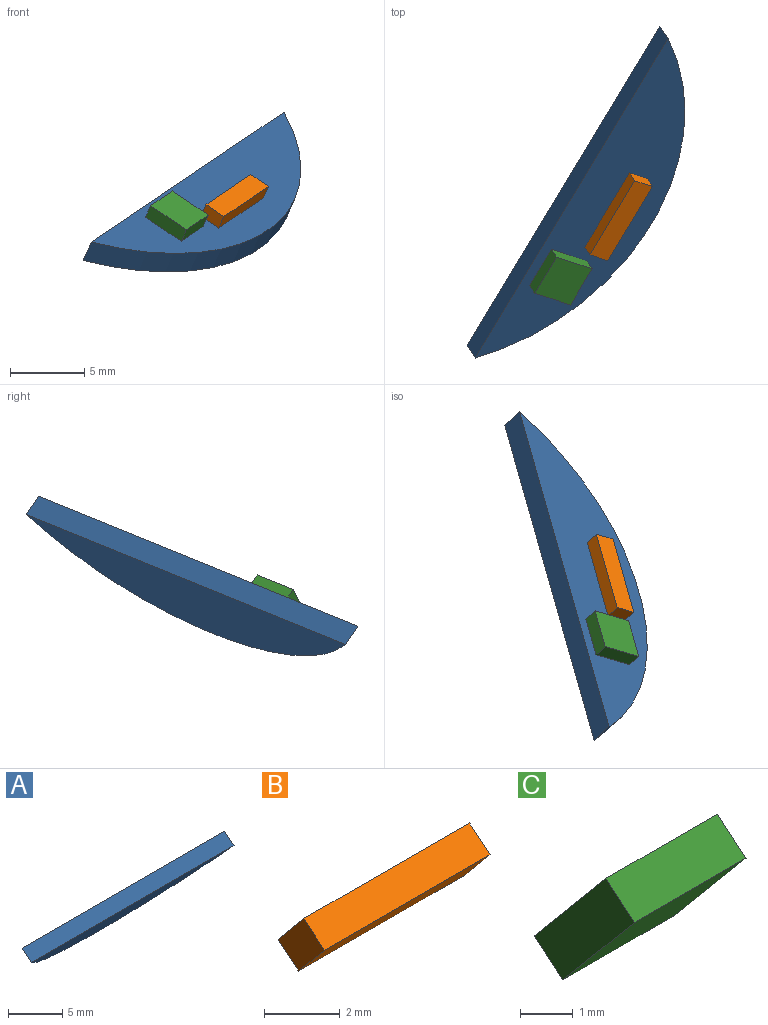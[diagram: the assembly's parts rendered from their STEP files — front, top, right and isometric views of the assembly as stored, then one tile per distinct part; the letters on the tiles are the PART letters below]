
ASSEMBLY  parts=3 mates=2
PART A: 4 faces, bbox 26.5x5.5x6.1 mm
  f0: cylinder r=16.5mm len=26.53mm, axis (0,0.77,0.64), area 49.3mm2, adj f1,f2,f3
  f1: plane 26.53x1.23mm, normal (0,-0.64,0.77), area 42.4mm2, adj f0,f2,f3
  f2: plane 26.53x5.12mm, normal (0,-0.77,-0.64), area 124mm2, adj f0,f1
  f3: plane 26.53x5.12mm, normal (0,0.77,0.64), area 124mm2, adj f0,f1
PART B: 6 faces, bbox 6.2x1.7x1.8 mm
  f0: plane 1.79x1.73mm, normal (1,0,0), area 1.5mm2, adj f1,f3,f4,f5
  f1: plane 6.16x0.77mm, normal (0,0.64,-0.77), area 6.2mm2, adj f0,f2,f4,f5
  f2: plane 1.79x1.73mm, normal (-1,0,0), area 1.5mm2, adj f1,f3,f4,f5
  f3: plane 6.16x0.77mm, normal (0,-0.64,0.77), area 6.2mm2, adj f0,f2,f4,f5
  f4: plane 6.16x1.15mm, normal (0,0.77,0.64), area 9.2mm2, adj f0,f1,f2,f3
  f5: plane 6.16x1.15mm, normal (0,-0.77,-0.64), area 9.2mm2, adj f0,f1,f2,f3
PART C: 6 faces, bbox 3x2.7x2.9 mm
  f0: plane 3x0.77mm, normal (0,0.64,-0.77), area 3mm2, adj f1,f3,f4,f5
  f1: plane 2.94x2.69mm, normal (-1,0,0), area 3mm2, adj f0,f2,f4,f5
  f2: plane 3x0.77mm, normal (0,-0.64,0.77), area 3mm2, adj f1,f3,f4,f5
  f3: plane 2.94x2.69mm, normal (1,0,0), area 3mm2, adj f0,f2,f4,f5
  f4: plane 3x2.3mm, normal (0,0.77,0.64), area 9mm2, adj f0,f1,f2,f3
  f5: plane 3x2.3mm, normal (0,-0.77,-0.64), area 9mm2, adj f0,f1,f2,f3
PLACE A rot(axis=(0.23,-0.04,-0.97),125.1deg) t=(26.06,-20.08,45.56)mm
PLACE B rot(axis=(0.78,0.27,0.56),109.3deg) t=(73.44,-35.68,13.6)mm
PLACE C rot(axis=(-0.92,0.36,0.17),106.3deg) t=(85.63,-54.23,110.73)mm
MATE fastened B.f5 <-> A.f3  axis (-0.35,0.53,-0.77) through (65.17,-51.12,63.8)mm
MATE fastened C.f4 <-> A.f3  axis (-0.35,0.53,-0.77) through (61.29,-55.17,62.8)mm
